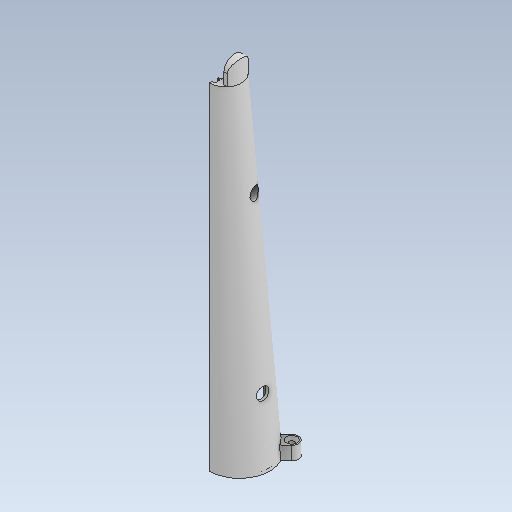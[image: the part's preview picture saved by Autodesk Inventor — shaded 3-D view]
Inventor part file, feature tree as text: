
AUTODESK INVENTOR PART (.ipt)
format: ipt  version: 2021 (Build 250183000, 183)  size: 861,184 bytes
history: native  units: mm
features: sketch x35, extrude x30, plane x15, fillet x4, hole x3, loft x2, revolve x2, other x1, thread x1
ambient origin geometry x8: Origin, YZ Plane, XZ Plane, XY Plane, X Axis, Y Axis, Z Axis, Center Point
bodies: Body1 (feature_tree)
feature tree (93):
  other  "Sólido1"
  plane  "Plano de trabajo1"
  plane  "Plano de trabajo2"
  plane  "Plano de trabajo4"
  plane  "Plano de trabajo5"
  plane  "Plano de trabajo6"
  sketch  "Boceto1"  dims[d1=250.0mm d2=0.0mm d3=-80.0mm d4=-110.0mm]
  sketch  "Boceto2"  dims[d5=-140.0mm d7=-0.0mm d8=2.0mm]
  sketch  "Boceto3"  dims[d9=140.0mm d10=250.0mm]
  sketch  "Boceto4"  dims[d11=24.0mm d22=0.0mm d23=90.0deg d24=0.0mm d25=90.0deg]
  sketch  "Boceto6"  dims[d44=45.0mm d49=29.11157mm]
  sketch  "Boceto7"  dims[d50=29.11157mm d53=29.11157mm]
  loft  "Solevación1"
  fillet  "Empalme2"  [1 undecoded]
  extrude  "Extrusión1"  TaperAngle=0.0deg  [1 undecoded]
  fillet  "Empalme5"  Radius=2.0mm
  plane  "Plano de trabajo7"
  extrude  "Extrusión2"  Depth=250.0mm
  plane  "Plano de trabajo8"
  plane  "Plano de trabajo9"
  loft  "Solevación9"
  plane  "Plano de trabajo10"
  extrude  "Extrusión3"  Depth=29.11157mm
  plane  "Plano de trabajo11"
  revolve  "Revolución1"  [1 undecoded]
  revolve  "Revolución2"  [1 undecoded]
  extrude  "Extrusión4"  Depth=32.5mm
  plane  "Plano de trabajo12"
  extrude  "Extrusión5"  Depth=44.747934mm
  plane  "Plano de trabajo13"
  plane  "Plano de trabajo14"
  extrude  "Extrusión6"  Depth=42.747934mm
  extrude  "Extrusión7"  Depth=42.747934mm
  extrude  "Extrusión8"  Depth=13.0mm
  extrude  "Extrusión11"  Depth=7.75mm
  extrude  "Extrusión9"  Depth=7.75mm
  extrude  "Extrusión10"  Depth=16.0mm
  extrude  "Extrusión12"  Depth=12.0mm
  sketch  "Boceto30"  dims[d160=-19.75mm d161=0.0mm d163=0.0mm d164=2.0mm]
  extrude  "Extrusión13"  Depth=7.75mm
  extrude  "Extrusión14"  Depth=7.75mm
  extrude  "Extrusión15"  TaperAngle=0.0deg  [1 undecoded]
  hole  "Agujero1"  [1 undecoded]
  thread  "Rosca1"  [1 undecoded]
  extrude  "Extrusión16"  Depth=2.0mm
  plane  "Plano de trabajo16"
  extrude  "Extrusión17"  TaperAngle=0.0deg  [1 undecoded]
  extrude  "Extrusión18"  TaperAngle=0.0deg  [1 undecoded]
  fillet  "Empalme6"  [1 undecoded]
  fillet  "Empalme7"  Radius=2.0mm
  plane  "Plano de trabajo17"
  sketch  "Boceto46"  dims[d185=2.0mm d187=1.0mm]
  hole  "Agujero2"  [1 undecoded]
  hole  "Agujero3"  [1 undecoded]
  extrude  "Extrusión21"  [1 undecoded]
  sketch  "Boceto44"  dims[d181=0.75mm d182=0.25mm]
  extrude  "Extrusión23"  Depth=0.75mm
  sketch  "Boceto47"  dims[d189=3.0mm d190=2.0mm]
  extrude  "Extrusión22"  Depth=1.0mm
  sketch  "Boceto45"  dims[d183=1.0mm d184=0.25mm]
  extrude  "Extrusión32"  Depth=17.453293mm
  extrude  "Extrusión29"  Depth=0.75mm
  extrude  "Extrusión30"  Depth=0.25mm
  extrude  "Extrusión31"  Depth=0.25mm
  extrude  "Extrusión26"  Depth=1.0mm
  extrude  "Extrusión27"  Depth=3.0mm
  extrude  "Extrusión28"  Depth=10.0mm
  sketch  "Boceto49"  dims[d191=2.0mm d192=0.25mm d193=0.25mm d194=90.0deg d196=4.381635mm d197=0.0mm d198=-48.35mm d199=12.0mm d200=20.0mm d201=9.0mm d202=9.0mm d203=2.0mm d204=201.65mm d205=0.0mm d206=0.5mm d207=0.25mm d208=-7.5mm d209=100.0mm d210=0.0mm d211=35.0mm d212=0.0mm d213=210.0mm d214=0.0mm d215=2.0mm d216=1.059493mm d217=6.5mm d218=1.059493mm d219=5.0mm d220=2.0mm d221=0.0mm d222=2.0mm d223=6.5mm d224=1.059493mm d225=5.0mm d226=4.85mm d227=2.0mm d228=0.0mm d229=6.0mm d230=10.0mm d231=3.0mm d232=11.0mm d233=10.5mm d235=30.0deg d236=4.75mm d237=0.0mm d238=-17.0mm d239=100.0mm d240=0.0mm d241=6.5mm d242=1.65mm d243=3.3mm d244=15.6mm d245=2.0mm d247=16.0mm d248=2.0mm d249=0.0mm d250=4.5mm d251=0.75mm d252=2.5mm d253=1.0mm d254=11.0mm d255=17.453293mm d256=2.939597mm d257=0.75mm d258=0.75mm d259=0.25mm d260=1.0mm d261=0.25mm d262=2.0mm d263=1.0mm d264=3.0mm d265=2.0mm d266=2.0mm d267=0.25mm d268=0.25mm d269=40.0mm d270=1.0mm d271=1.0mm d272=7.75mm d273=0.5mm d274=8.5mm d275=90.0deg d276=0.0mm d277=17.75mm d280=22.5mm d281=2.0mm d282=0.0mm d283=0.0mm d292=2.0mm d293=0.0mm d296=3.5mm d297=0.0mm d299=4.0mm d300=3.708mm d301=3.023mm d302=2.0mm d303=14.3117mm d304=16.0mm d305=0.0mm d306=16.0mm d307=0.0mm d314=6.0mm d315=19.2mm d316=6.0mm d317=19.2mm d318=13.0mm d320=6.0mm d321=19.2mm d322=13.0mm d323=6.0mm d324=19.2mm d325=13.0mm d326=7.0mm d332=10.0mm d333=0.0mm d335=-41.6mm d336=4.0mm d337=1.0mm d338=9.0mm d339=4.0mm d340=1.0mm d341=9.0mm d342=4.0mm d343=5.2mm d344=4.0mm d345=0.0mm d346=15.0mm d347=5.0mm d349=5.0mm d351=0.0mm d352=45.0mm d354=10.0mm d355=10.0mm d356=0.0mm d357=15.0mm d358=0.0mm d359=2.0mm d363=50.4125mm d376=14.059493mm d377=2.0mm d378=0.0mm d379=2.0mm d380=11.25mm d381=90.0mm d382=290.0mm d383=14.059493mm d384=100.825mm d390=30.940507mm d391=2.0mm d392=100.825mm d393=14.790546mm d394=2.0mm d395=3.0mm d396=6.0mm d397=4.0mm d398=4.0mm d399=4.0mm d400=8.128453mm d401=12.0mm d402=4.45mm d403=2.5mm d404=1.65mm d405=1.65mm d406=1.0mm d407=2.0mm d408=2.0mm d409=0.0mm d411=50.4125mm d412=6.0mm d418=13.059493mm d419=6.5mm d420=6.5mm d421=50.4125mm d422=126.03125mm d423=0.0mm d424=15.0mm d425=5.0mm d426=5.0mm d427=0.0mm d428=45.0mm d429=10.0mm d430=2.0mm d431=4.0mm d432=6.0mm d433=8.0mm d434=2.0mm d435=90.0deg d436=20.0mm d437=0.0mm d438=4.0mm d439=6.0mm d440=8.0mm d441=2.0mm d442=90.0deg d443=20.0mm d444=0.0mm d446=10.0mm d447=3.0mm d448=11.5mm d450=9.0mm d451=9.0mm d452=90.0mm d453=750.0mm d454=22.5mm d455=43.0mm d456=44.0mm d457=14.059493mm d458=11.25mm d459=2.0mm d460=0.0mm d461=22.5mm d462=43.0mm d463=7.059493mm d464=3.0mm d465=6.0mm d466=3.0mm d467=6.0mm d468=180.0mm d469=0.0mm d470=180.0mm d471=0.0mm d472=4.5mm d473=10.0mm d474=0.0mm d475=7.0mm d476=0.0mm d477=0.0mm d478=0.0mm d479=6.0mm d480=0.0mm d481=14.059493mm d482=250.0mm d483=2.0mm d484=0.0mm d485=4.2mm d486=4.2mm d487=4.2mm d488=7.0mm d489=0.0mm d490=2.0mm d491=0.0mm d492=4.0mm d493=4.0mm d494=0.0mm d495=0.0mm d496=0.0mm d497=0.0mm]
  extrude  "Extrusión24"  Depth=10.0mm
  extrude  "Extrusión25"  TaperAngle=90.0deg  [1 undecoded]
  sketch  "Boceto9"  dims[d59=29.11157mm d61=29.11157mm]
  sketch  "Boceto10"  dims[d65=22.5mm d66=32.5mm]
  sketch  "Boceto15"  dims[d67=22.5mm d90=44.747934mm]
  sketch  "Boceto16"  dims[d91=42.747934mm d93=42.747934mm]
  sketch  "Boceto17"  dims[d96=0.0mm d97=90.0deg d98=0.0mm d99=90.0deg d100=0.0mm d101=90.0deg d102=0.0mm d103=90.0deg d112=42.747934mm]
  sketch  "Boceto18"  dims[d115=5.0mm d120=13.0mm]
  sketch  "Boceto19"  dims[d121=6.5mm d124=7.75mm]
  sketch  "Boceto20"  dims[d125=7.75mm d126=7.75mm]
  sketch  "Boceto21"  dims[d127=7.75mm d130=16.0mm]
  sketch  "Boceto22"  dims[d131=0.0mm d132=12.0mm]
  sketch  "Boceto24"  dims[d133=12.0mm d134=7.75mm]
  sketch  "Boceto25"  dims[d135=6.5mm d136=7.75mm]
  sketch  "Boceto26"  dims[d137=15.0mm d138=0.0mm]
  sketch  "Boceto27"  dims[d146=-8.5mm d147=30.0mm d148=2.0mm]
  sketch  "Boceto28"  dims[d149=25.12mm d150=2.0mm]
  sketch  "Boceto29"  dims[d151=10.357mm d156=0.0mm d157=90.0deg d158=0.0mm d159=90.0deg]
  sketch  "Boceto31"  dims[d165=15.0mm d166=4.0mm]
  sketch  "Boceto36"  dims[d167=30.0mm d168=12.0mm]
  sketch  "Boceto37"  dims[d169=0.0mm d170=-7.25mm]
  sketch  "Boceto38"  dims[d171=4.5mm d172=0.75mm]
  sketch  "Boceto39"  dims[d173=2.5mm d174=1.0mm]
  sketch  "Boceto40"  dims[d176=11.0mm d177=17.453293mm]
  sketch  "Boceto41"  dims[d179=2.939597mm d180=0.75mm]
note: 14 required parameter values undecoded (feature->parameter linkage not recoverable at this tier; creation-order binding heuristic only, values carry confidence <= 0.55)